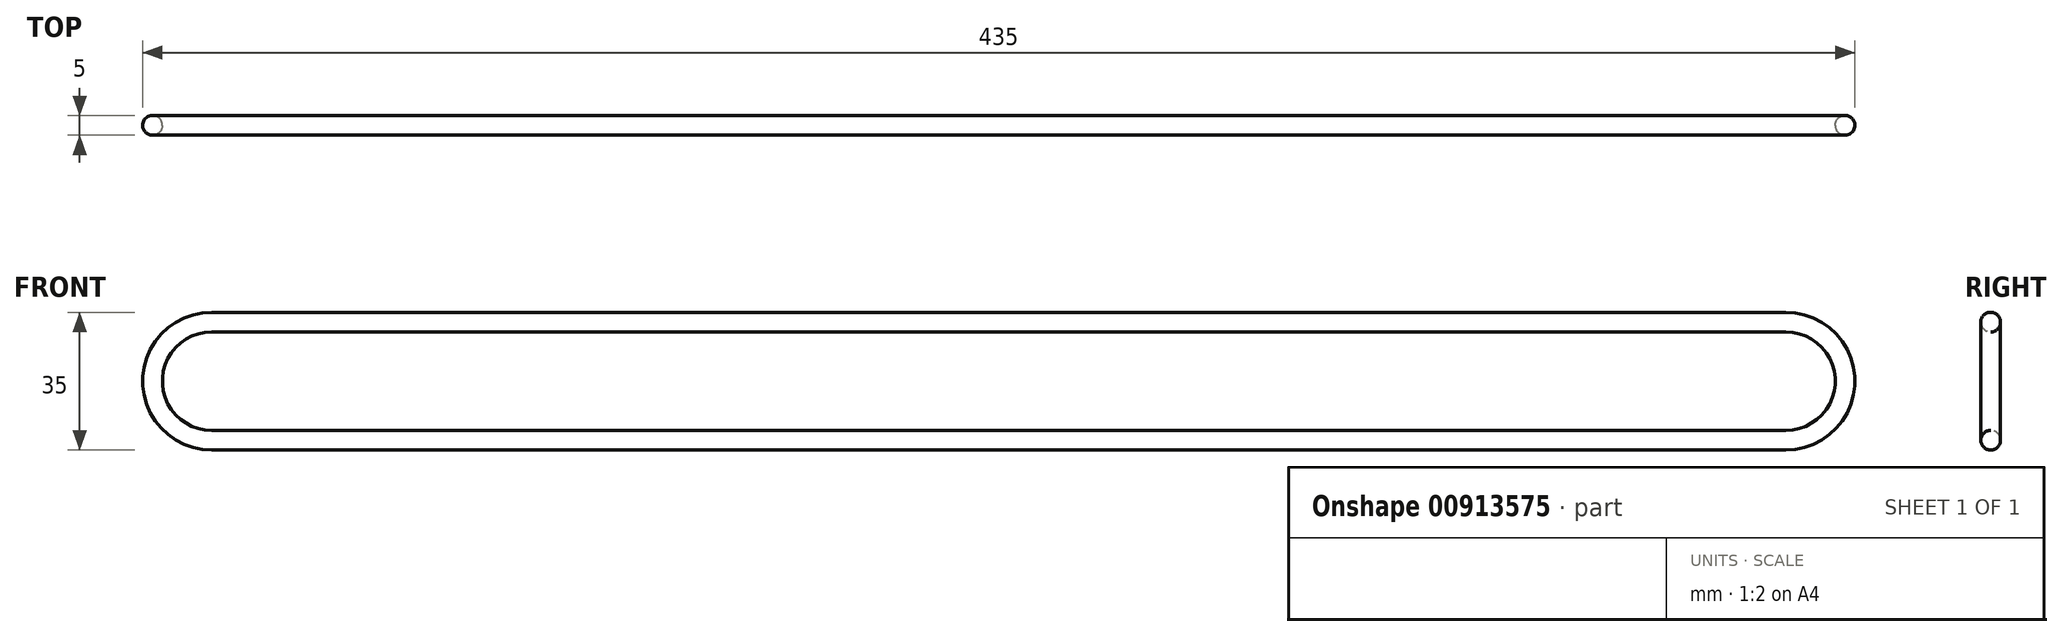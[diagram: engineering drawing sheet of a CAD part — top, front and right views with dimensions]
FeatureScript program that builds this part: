
annotation { "Feature Type Name" : "Feature", "Feature Type Description" : "" }
export const myFeature = defineFeature(function(context is Context, id is Id, definition is map)
    precondition{}
    {
        {
            var Q0;
            Q0=qCreatedBy(makeId("Front.planeOp"),FACE);
            var sketch = newSketch(context, id + "F0", { "sketchPlane" : qUnion([Q0])});
            skLineSegment(sketch, "E0", {"start": v(400, 15) * mm, "end": v(0, 15) * mm});
            skArc(sketch, "E1", {"start": v(0, 15) * mm, "mid": v(-15, 0) * mm, "end": v(0, -15) * mm});
            skLineSegment(sketch, "E2", {"start": v(0, -15) * mm, "end": v(400, -15) * mm});
            skArc(sketch, "E3", {"start": v(400, -15) * mm, "mid": v(415, 0) * mm, "end": v(400, 15) * mm});
            skSolve(sketch);
        }
        {
            var Q0;
            Q0=qCreatedBy(makeId("Right.planeOp"),FACE);
            var sketch = newSketch(context, id + "F1", { "sketchPlane" : qUnion([Q0])});
            skCircle(sketch, "E4", {"center": v(0, 15) * mm, "radius": 2.5 * mm});
            skSolve(sketch);
        }
        {
            var Q0;
            Q0 = qSketchRegion(id + "F1", true);
            var Q1;
            Q1 = qConstructionFilter(qBodyType(qCreatedBy(id + "F0" ,EDGE), BodyType.WIRE), ConstructionObject.NO);
            sweep(context, id + "F2", {"profiles" : qUnion([Q0]), "path" : qUnion([Q1])});
        }
    });
